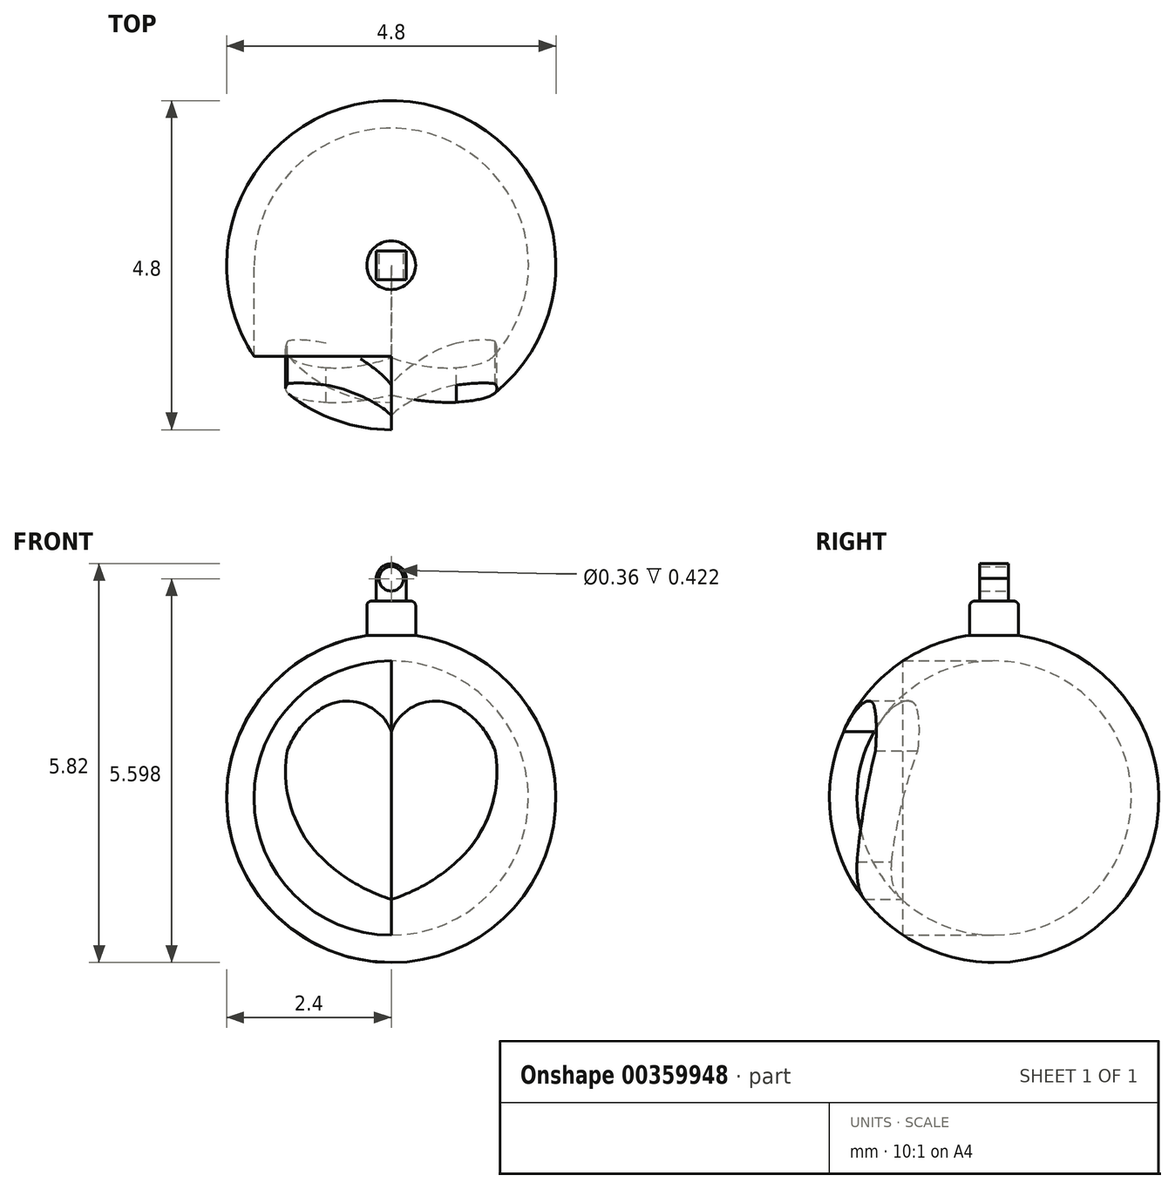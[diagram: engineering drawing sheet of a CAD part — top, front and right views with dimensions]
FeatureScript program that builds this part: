
annotation { "Feature Type Name" : "Feature", "Feature Type Description" : "" }
export const myFeature = defineFeature(function(context is Context, id is Id, definition is map)
    precondition{}
    {
        {
            var Q0;
            Q0=qCreatedBy(makeId("Front.planeOp"),FACE);
            var sketch = newSketch(context, id + "F0", { "sketchPlane" : qUnion([Q0])});
            skCircle(sketch, "E0", {"center": v(0, 0) * mm, "radius": 2 * mm});
            skCircle(sketch, "E1", {"center": v(0, 0) * mm, "radius": 2.4 * mm});
            skLineSegment(sketch, "E2", {"start": v(0.36, 2.87) * mm, "end": v(0.36, 2.37) * mm});
            skLineSegment(sketch, "E3", {"start": v(0, 2.87) * mm, "end": v(0, -2.4) * mm});
            skLineSegment(sketch, "E4", {"start": v(-0.36, 2.87) * mm, "end": v(-0.36, 2.37) * mm});
            skLineSegment(sketch, "E5", {"start": v(-0.36, 2.87) * mm, "end": v(0.36, 2.87) * mm});
            skLineSegment(sketch, "E6", {"start": v(-0.22, 2.87) * mm, "end": v(-0.22, 3.2) * mm});
            skLineSegment(sketch, "E7", {"start": v(0.22, 2.87) * mm, "end": v(0.22, 3.2) * mm});
            skArc(sketch, "E8", {"start": v(0.22, 3.2) * mm, "mid": v(0, 3.42) * mm, "end": v(-0.22, 3.2) * mm});
            skCircle(sketch, "E9", {"center": v(0, 3.2) * mm, "radius": 0.18 * mm});
            skLineSegment(sketch, "E10", {"start": v(0, 3.42) * mm, "end": v(0, 2.87) * mm});
            skArc(sketch, "E11", {"start": v(0.95, 1.34) * mm, "mid": v(0.4, 1.37) * mm, "end": v(0, 0.97) * mm});
            skArc(sketch, "E12", {"start": v(1.51, 0.69) * mm, "mid": v(1.3, 1.07) * mm, "end": v(0.95, 1.34) * mm});
            skArc(sketch, "E13", {"start": v(0.95, -0.93) * mm, "mid": v(1.45, -0.2) * mm, "end": v(1.51, 0.69) * mm});
            skArc(sketch, "E14", {"start": v(0, -1.48) * mm, "mid": v(0.5, -1.26) * mm, "end": v(0.95, -0.93) * mm});
            skArc(sketch, "E15.MirrorCS", {"start": v(-0.95, 1.34) * mm, "mid": v(-0.4, 1.37) * mm, "end": v(0, 0.97) * mm});
            skArc(sketch, "E16.MirrorCS", {"start": v(-1.51, 0.69) * mm, "mid": v(-1.3, 1.07) * mm, "end": v(-0.95, 1.34) * mm});
            skArc(sketch, "E17.MirrorCS", {"start": v(-0.95, -0.93) * mm, "mid": v(-1.45, -0.2) * mm, "end": v(-1.51, 0.69) * mm});
            skArc(sketch, "E18.MirrorCS", {"start": v(0, -1.48) * mm, "mid": v(-0.5, -1.26) * mm, "end": v(-0.95, -0.93) * mm});
            skSolve(sketch);
        }
        {
            var Q0;
            {var subQ0=sQuery(id+"F0.wireOp",EDGE,"E2");Q0=makeQuery(id+"F0.imprint","IMPRINT",FACE,{"disambiguationData":[TD([[makeQuery(id+"F0.imprint","IMPRINT",EDGE,{"derivedFrom":subQ0}),-1.0]])]});}
            var Q1;
            {var subQ0=sQuery(id+"F0.wireOp",EDGE,"E3");var subQ1=sQuery(id+"F0.wireOp",EDGE,"E0");var subQ2=makeQuery(id+"F0.imprint","INTERSECT",VERTEX,{"disambiguationData":[OD(0.0)],"derivedFrom":[subQ1,subQ0]});Q1=makeQuery(id+"F0.imprint","IMPRINT",FACE,{"disambiguationData":[TD([[makeQuery(id+"F0.imprint","IMPRINT",EDGE,{"disambiguationData":[TD([[subQ2,1.0]])],"derivedFrom":subQ1}),-1.0]])]});}
            var Q2;
            Q2=sQuery(id+"F0.wireOp",EDGE,"E3");
            revolve(context, id + "F1", {"entities" : qUnion([Q0, Q1]), "axis" : qUnion([Q2]), "revolveType" : RevolveType.FULL});
        }
        {
            var Q0;
            {var subQ5=sQuery(id+"F0.wireOp",EDGE,"E7");Q0=makeQuery(id+"F0.imprint","IMPRINT",FACE,{"disambiguationData":[TD([[makeQuery(id+"F0.imprint","IMPRINT",EDGE,{"derivedFrom":subQ5}),1.0]])]});}
            var Q1;
            {var subQ5=sQuery(id+"F0.wireOp",EDGE,"E6");Q1=makeQuery(id+"F0.imprint","IMPRINT",FACE,{"disambiguationData":[TD([[makeQuery(id+"F0.imprint","IMPRINT",EDGE,{"derivedFrom":subQ5}),-1.0]])]});}
            extrude(context, id + "F2", {"entities" : qUnion([Q0, Q1]), "operationType" : NewBodyOperationType.ADD, "endBound" : BoundingType.SYMMETRIC, "depth" : 0.42 * mm});
        }
        {
            var Q0;
            {var subQ0=sQuery(id+"F0.wireOp",EDGE,"E15.MirrorCS");Q0=makeQuery(id+"F0.imprint","IMPRINT",FACE,{"disambiguationData":[TD([[makeQuery(id+"F0.imprint","IMPRINT",EDGE,{"derivedFrom":subQ0}),-1.0]])]});}
            var Q1;
            {var subQ0=sQuery(id+"F0.wireOp",EDGE,"E11");Q1=makeQuery(id+"F0.imprint","IMPRINT",FACE,{"disambiguationData":[TD([[makeQuery(id+"F0.imprint","IMPRINT",EDGE,{"derivedFrom":subQ0}),1.0]])]});}
            extrude(context, id + "F3", {"entities" : qUnion([Q0, Q1]), "operationType" : NewBodyOperationType.REMOVE, "depth" : 4.11 * mm});
        }
        {
            var Q0;
            Q0=makeQuery(id+"F1.opRevolve","SWEPT_EDGE",EDGE,{"disambiguationData":[OSD([sQuery(id+"F0.wireOp",EDGE,"E2"),sQuery(id+"F0.wireOp",EDGE,"E5")])]});
            fillet(context, id + "F4", {"entities" : qUnion([Q0]), "radius" : 0.07 * mm, "tangentPropagation" : true, "allowEdgeOverflow" : false});
        }
    });
